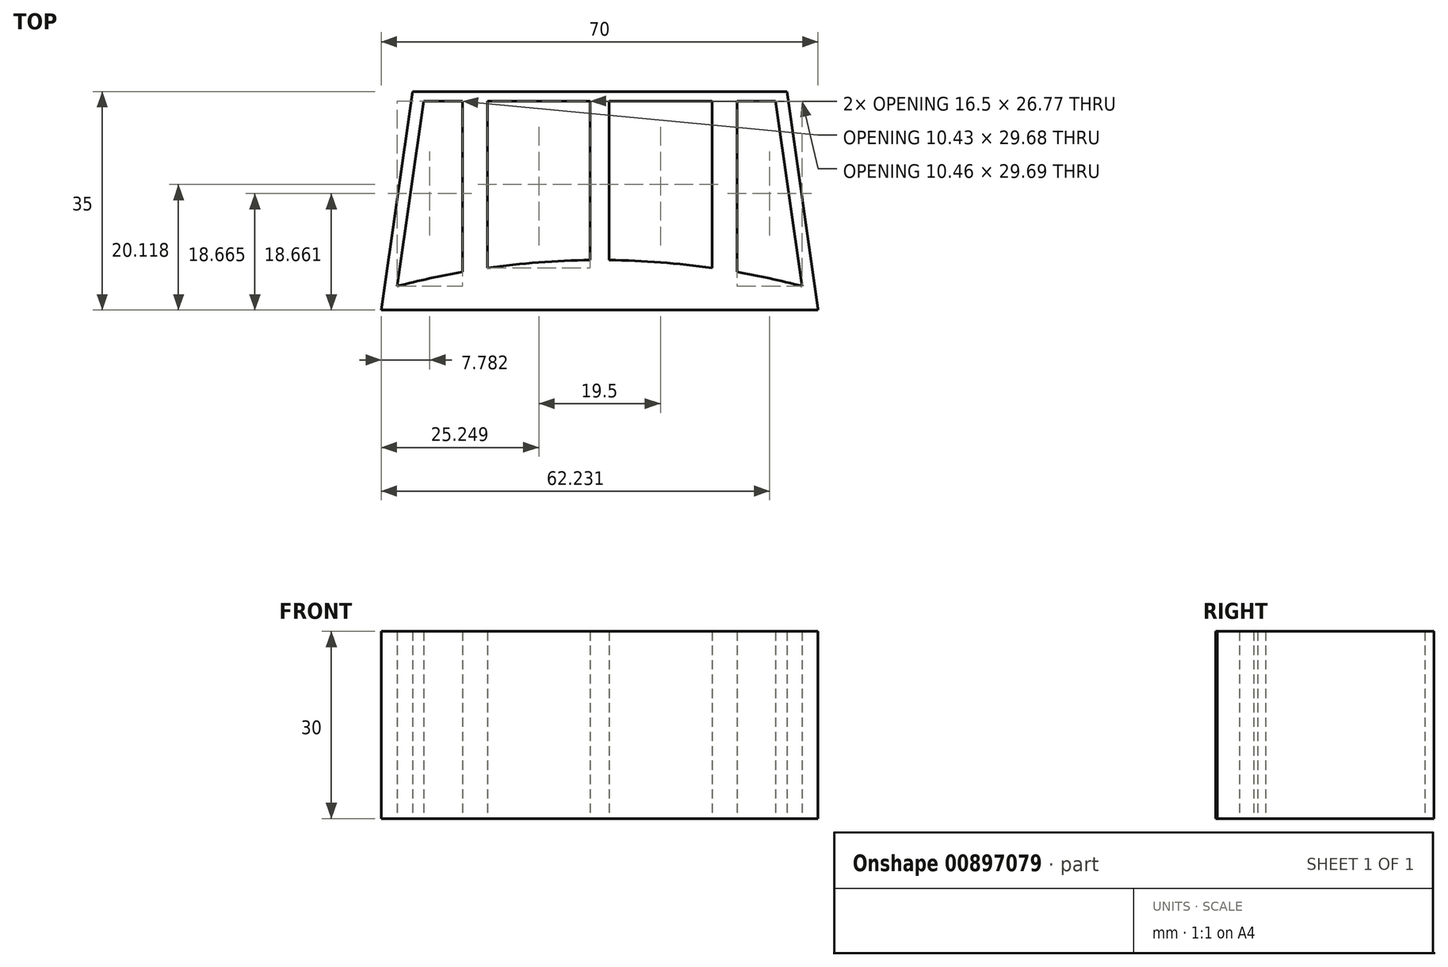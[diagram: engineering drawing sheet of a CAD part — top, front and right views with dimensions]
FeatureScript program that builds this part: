
annotation { "Feature Type Name" : "Feature", "Feature Type Description" : "" }
export const myFeature = defineFeature(function(context is Context, id is Id, definition is map)
    precondition{}
    {
        {
            var Q0;
            Q0=qCreatedBy(makeId("Top.planeOp"),FACE);
            var sketch = newSketch(context, id + "F0", { "sketchPlane" : qUnion([Q0])});
            skLineSegment(sketch, "E0.bottom", {"start": v(-32.81, 18.73) * mm, "end": v(37.19, 18.73) * mm});
            skLineSegment(sketch, "E0.top", {"start": v(-32.81, -16.27) * mm, "end": v(37.19, -16.27) * mm});
            skLineSegment(sketch, "E0.left", {"start": v(-32.81, 18.73) * mm, "end": v(-32.81, -16.27) * mm});
            skLineSegment(sketch, "E0.right", {"start": v(37.19, 18.73) * mm, "end": v(37.19, -16.27) * mm});
            skSolve(sketch);
        }
        {
            var Q0;
            Q0=makeQuery(id+"F0.imprint","IMPRINT",FACE,{"disambiguationData":[TD([[makeQuery(id+"F0.imprint","IMPRINT",EDGE,{"derivedFrom":sQuery(id+"F0.wireOp",EDGE,"E0.bottom")}),-1.0]])]});
            var sketch = newSketch(context, id + "F1", { "sketchPlane" : qUnion([Q0])});
            skLineSegment(sketch, "E1", {"start": v(-32.81, -16.27) * mm, "end": v(-27.81, 18.73) * mm});
            skLineSegment(sketch, "E2", {"start": v(37.22, -16.27) * mm, "end": v(32.19, 18.73) * mm});
            skSolve(sketch);
        }
        {
            var Q0;
            {var subQ1=sQuery(id+"F1.wireOp",EDGE,"E1");Q0=makeQuery(id+"F1.imprint","IMPRINT",FACE,{"disambiguationData":[TD([[makeQuery(id+"F1.imprint","IMPRINT",EDGE,{"derivedFrom":subQ1}),-1.0]])]});}
            extrude(context, id + "F2", {"entities" : qUnion([Q0]), "depth" : 30 * mm, "offsetDistance" : 25 * mm});
        }
        {
            var Q0;
            Q0=makeQuery(id+"F0.imprint","IMPRINT",FACE,{"disambiguationData":[TD([[makeQuery(id+"F0.imprint","IMPRINT",EDGE,{"derivedFrom":sQuery(id+"F0.wireOp",EDGE,"E0.bottom")}),-1.0]])]});
            var sketch = newSketch(context, id + "F3", { "sketchPlane" : qUnion([Q0])});
            skArc(sketch, "E3", {"start": v(37.19, -16.27) * mm, "mid": v(2.19, -11.27) * mm, "end": v(-32.81, -16.27) * mm});
            skSolve(sketch);
        }
        {
            var Q0;
            Q0=makeQuery(id+"F3.imprint","IMPRINT",FACE,{"disambiguationData":[TD([[makeQuery(id+"F3.imprint","IMPRINT",EDGE,{"derivedFrom":sQuery(id+"F3.wireOp",EDGE,"E3")}),1.0]])]});
            var Q1;
            Q1=sQuery(id+"F3.wireOp",EDGE,"E3");
            var Q2;
            Q2=sQuery(id+"F0.wireOp",EDGE,"E0.top");
            extrude(context, id + "F4", {"entities" : qUnion([Q0]), "operationType" : NewBodyOperationType.ADD, "surfaceEntities" : qUnion([Q1, Q2]), "depth" : 30 * mm, "offsetDistance" : 25 * mm});
        }
        {
            var Q0;
            Q0=qCreatedBy(makeId("Top.planeOp"),FACE);
            var sketch = newSketch(context, id + "F5", { "sketchPlane" : qUnion([Q0])});
            skLineSegment(sketch, "E4.0", {"start": v(34.65, -12.45) * mm, "end": v(30.38, 17.23) * mm});
            skLineSegment(sketch, "E5.0", {"start": v(-30.24, -12.44) * mm, "end": v(-26, 17.23) * mm});
            skLineSegment(sketch, "E6.0", {"start": v(-26, 17.23) * mm, "end": v(30.38, 17.23) * mm});
            skLineSegment(sketch, "E7", {"start": v(-19.81, 17.23) * mm, "end": v(-19.81, -10.17) * mm});
            skLineSegment(sketch, "E8", {"start": v(24.19, 17.23) * mm, "end": v(24.19, -10.17) * mm});
            skLineSegment(sketch, "E9", {"start": v(0.69, 17.23) * mm, "end": v(0.69, -8.27) * mm});
            skLineSegment(sketch, "E10", {"start": v(3.69, 17.23) * mm, "end": v(3.69, -11.4) * mm});
            skArc(sketch, "E11.0", {"start": v(34.65, -12.45) * mm, "mid": v(2.2, -8.27) * mm, "end": v(-30.24, -12.44) * mm});
            skLineSegment(sketch, "E12", {"start": v(-15.81, 17.23) * mm, "end": v(-15.81, -9.54) * mm});
            skLineSegment(sketch, "E13", {"start": v(20.19, 17.23) * mm, "end": v(20.19, -9.54) * mm});
            skSolve(sketch);
        }
        {
            var Q0;
            {var subQ0=sQuery(id+"F5.wireOp",EDGE,"E5.0");Q0=makeQuery(id+"F5.imprint","IMPRINT",FACE,{"disambiguationData":[TD([[makeQuery(id+"F5.imprint","IMPRINT",EDGE,{"derivedFrom":subQ0}),-1.0]])]});}
            var Q1;
            {var subQ0=sQuery(id+"F5.wireOp",EDGE,"E4.0");Q1=makeQuery(id+"F5.imprint","IMPRINT",FACE,{"disambiguationData":[TD([[makeQuery(id+"F5.imprint","IMPRINT",EDGE,{"derivedFrom":subQ0}),1.0]])]});}
            var Q2;
            {var subQ3=sQuery(id+"F5.wireOp",EDGE,"E13");Q2=makeQuery(id+"F5.imprint","IMPRINT",FACE,{"disambiguationData":[TD([[makeQuery(id+"F5.imprint","IMPRINT",EDGE,{"derivedFrom":subQ3}),-1.0]])]});}
            var Q3;
            {var subQ0=sQuery(id+"F5.wireOp",EDGE,"E9");Q3=makeQuery(id+"F5.imprint","IMPRINT",FACE,{"disambiguationData":[TD([[makeQuery(id+"F5.imprint","IMPRINT",EDGE,{"derivedFrom":subQ0}),-1.0]])]});}
            extrude(context, id + "F6", {"entities" : qUnion([Q0, Q1, Q2, Q3]), "operationType" : NewBodyOperationType.REMOVE, "depth" : 30 * mm, "offsetDistance" : 25 * mm});
        }
    });
